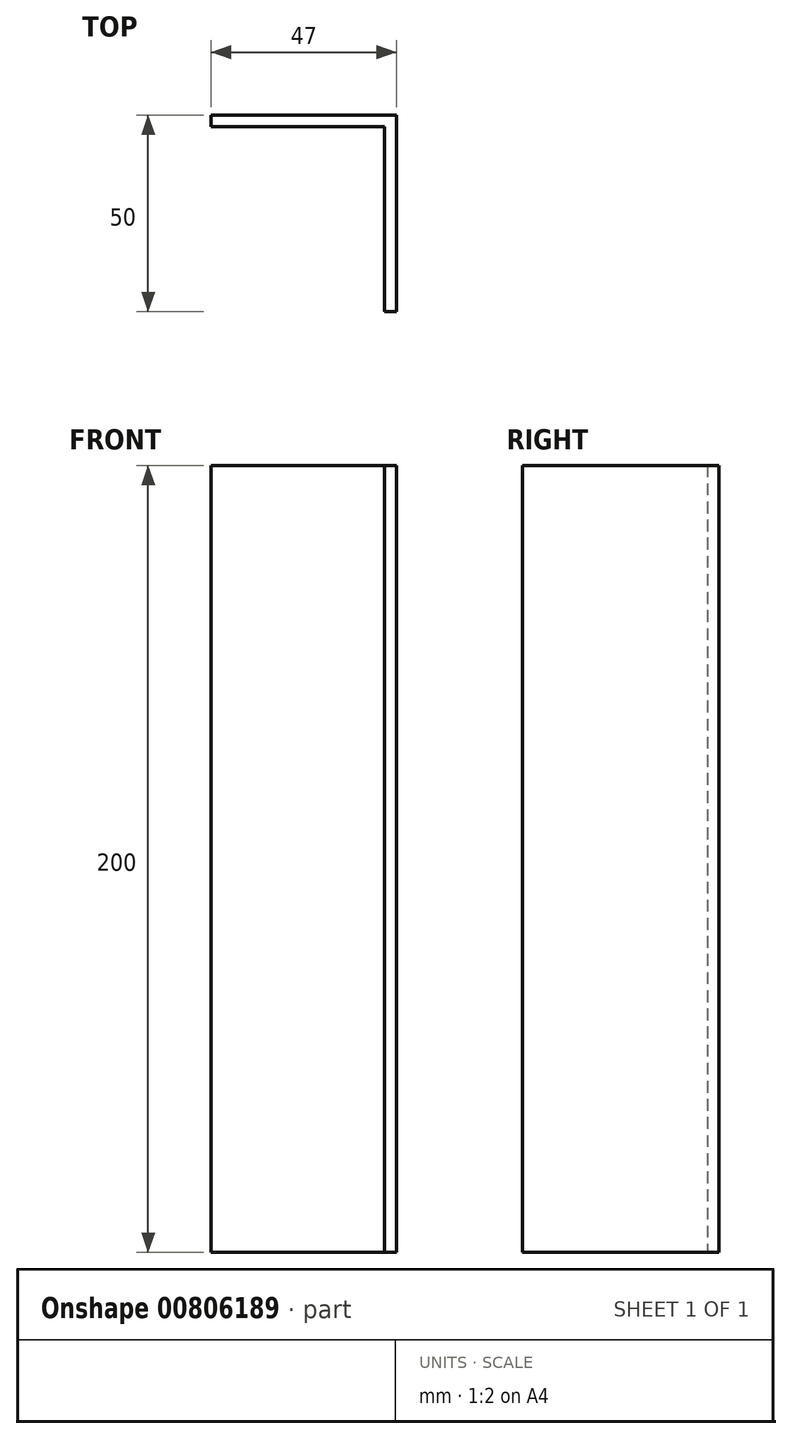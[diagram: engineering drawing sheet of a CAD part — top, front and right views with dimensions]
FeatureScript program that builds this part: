
annotation { "Feature Type Name" : "Feature", "Feature Type Description" : "" }
export const myFeature = defineFeature(function(context is Context, id is Id, definition is map)
    precondition{}
    {
        {
            var Q0;
            Q0=qCreatedBy(makeId("Top.planeOp"),FACE);
            var sketch = newSketch(context, id + "F0", { "sketchPlane" : qUnion([Q0])});
            skLineSegment(sketch, "E0.bottom", {"start": v(0, 0) * mm, "end": v(-3, 0) * mm});
            skLineSegment(sketch, "E0.top", {"start": v(0, 50) * mm, "end": v(-3, 50) * mm});
            skLineSegment(sketch, "E0.left", {"start": v(0, 0) * mm, "end": v(0, 50) * mm});
            skLineSegment(sketch, "E0.right", {"start": v(-3, 0) * mm, "end": v(-3, 50) * mm});
            skLineSegment(sketch, "E1", {"start": v(0, 50) * mm, "end": v(-47, 50) * mm});
            skLineSegment(sketch, "E2", {"start": v(-47, 50) * mm, "end": v(-47, 47) * mm});
            skLineSegment(sketch, "E3", {"start": v(-47, 47) * mm, "end": v(-3, 47) * mm});
            skSolve(sketch);
        }
        {
            var Q0;
            Q0=qSketchRegion(id+"F0",true);
            extrude(context, id + "F1", {"entities" : qUnion([Q0]), "depth" : 200 * mm, "offsetDistance" : 25 * mm});
        }
    });
